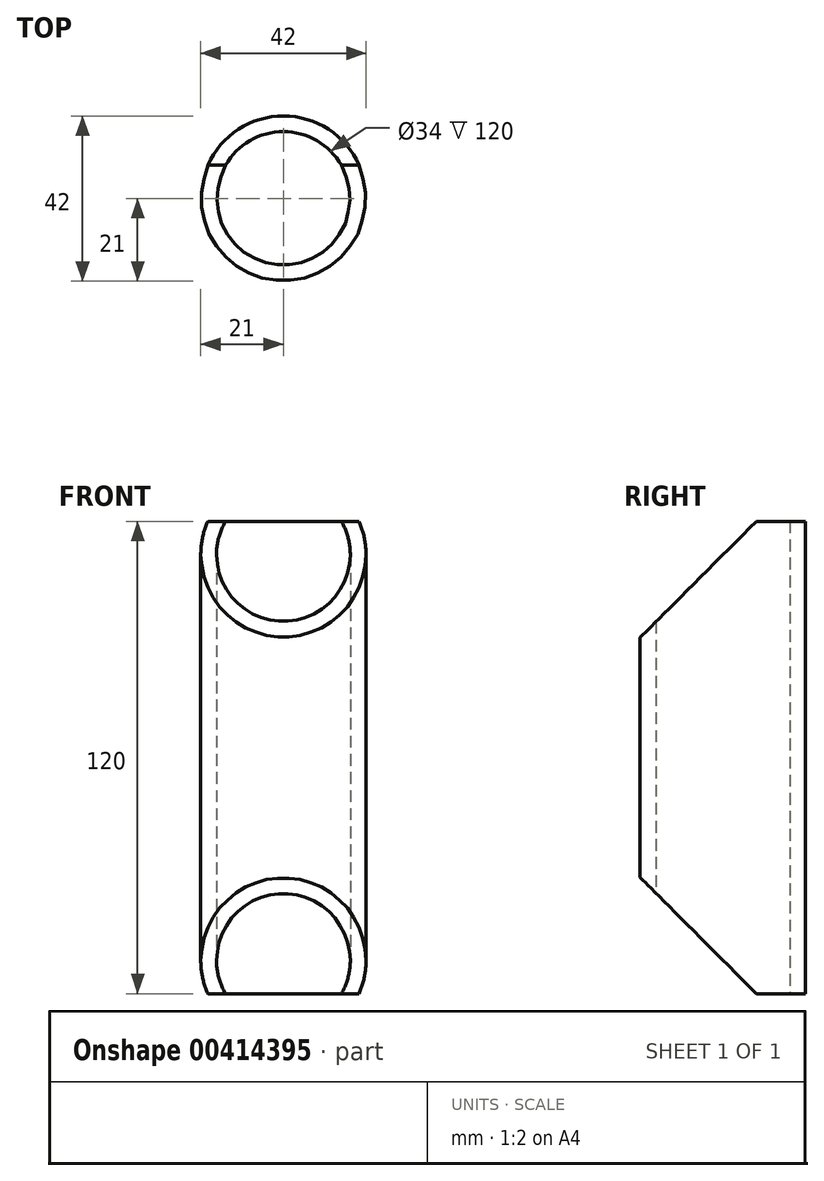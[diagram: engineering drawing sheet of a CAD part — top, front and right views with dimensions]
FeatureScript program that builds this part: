
annotation { "Feature Type Name" : "Feature", "Feature Type Description" : "" }
export const myFeature = defineFeature(function(context is Context, id is Id, definition is map)
    precondition{}
    {
        {
            var Q0;
            Q0=qCreatedBy(makeId("Top.planeOp"),FACE);
            var sketch = newSketch(context, id + "F0", { "sketchPlane" : qUnion([Q0])});
            skCircle(sketch, "E0", {"center": v(0, 0) * mm, "radius": 17 * mm});
            skCircle(sketch, "E1.0", {"center": v(0, 0) * mm, "radius": 21 * mm});
            skSolve(sketch);
        }
        {
            var Q0;
            Q0=qSketchRegion(id+"F0",true);
            extrude(context, id + "F1", {"entities" : qUnion([Q0]), "endBound" : BoundingType.SYMMETRIC, "offsetDistance" : 25 * mm, "depth" : 120 * mm});
        }
        {
            var Q0;
            Q0=qCreatedBy(makeId("Right.planeOp"),FACE);
            var sketch = newSketch(context, id + "F2", { "sketchPlane" : qUnion([Q0])});
            skLineSegment(sketch, "E2", {"start": v(8.5, 60) * mm, "end": v(-21, 30.5) * mm});
            skLineSegment(sketch, "E3", {"start": v(8.5, 60) * mm, "end": v(21, 60) * mm});
            skLineSegment(sketch, "E4", {"start": v(-21, 30.5) * mm, "end": v(-21, 70) * mm});
            skLineSegment(sketch, "E5", {"start": v(-21, 70) * mm, "end": v(21, 70) * mm});
            skLineSegment(sketch, "E6", {"start": v(21, 70) * mm, "end": v(21, 60) * mm});
            skPoint(sketch, "E7", {"position": v(0, 70) * mm});
            skLineSegment(sketch, "E8.MirrorCS", {"start": v(8.5, -60) * mm, "end": v(21, -60) * mm});
            skLineSegment(sketch, "E9.MirrorCS", {"start": v(-21, -70) * mm, "end": v(21, -70) * mm});
            skLineSegment(sketch, "E10.MirrorCS", {"start": v(8.5, -60) * mm, "end": v(-21, -30.5) * mm});
            skLineSegment(sketch, "E11.MirrorCS", {"start": v(21, -70) * mm, "end": v(21, -60) * mm});
            skLineSegment(sketch, "E12.MirrorCS", {"start": v(-21, -30.5) * mm, "end": v(-21, -70) * mm});
            skPoint(sketch, "E13.MirrorP", {"position": v(0, -70) * mm});
            skSolve(sketch);
        }
        {
            var Q0;
            Q0=qSketchRegion(id+"F2",true);
            extrude(context, id + "F3", {"entities" : qUnion([Q0]), "operationType" : NewBodyOperationType.REMOVE, "endBound" : BoundingType.SYMMETRIC, "oppositeDirection" : true, "depth" : 42 * mm});
        }
    });
